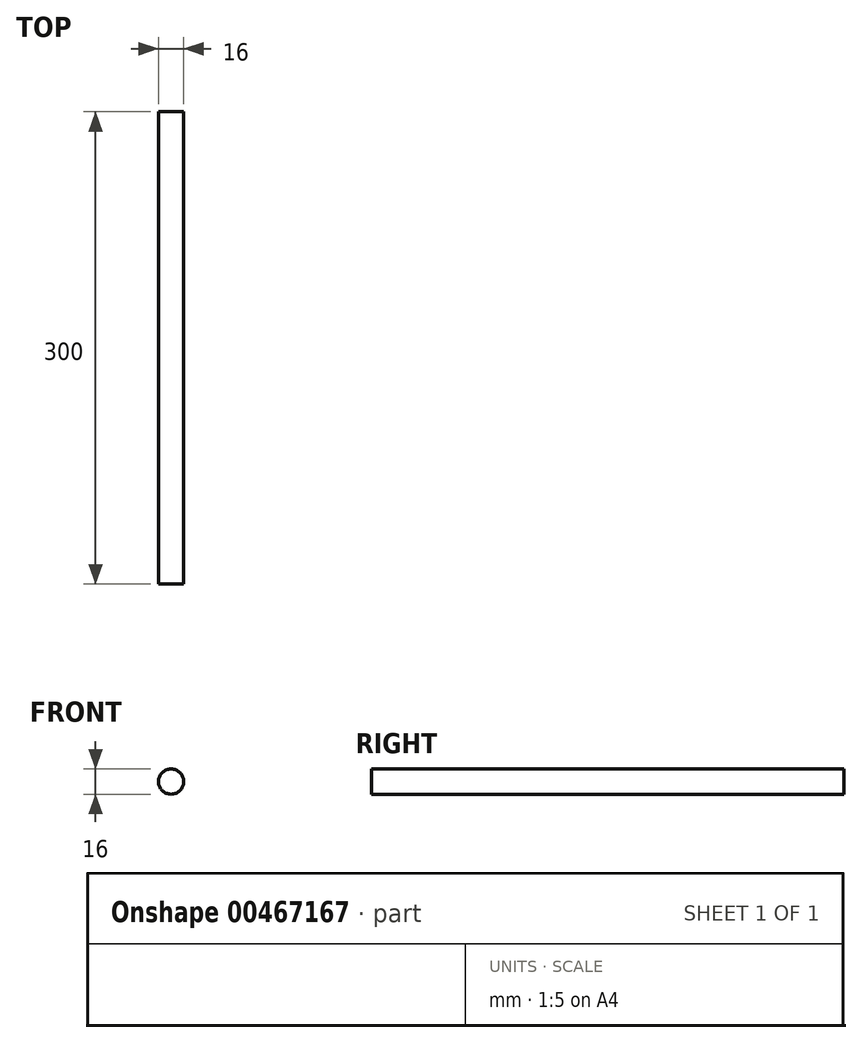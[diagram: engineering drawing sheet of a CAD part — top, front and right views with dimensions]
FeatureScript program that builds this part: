
annotation { "Feature Type Name" : "Feature", "Feature Type Description" : "" }
export const myFeature = defineFeature(function(context is Context, id is Id, definition is map)
    precondition{}
    {
        {
            assignVariable(context, id + "F0", {"name" : "Shaft_length", "anyValue" : 300 * mm});
        }
        {
            var Q0;
            Q0=qCreatedBy(makeId("Front.planeOp"),FACE);
            var sketch = newSketch(context, id + "F1", { "sketchPlane" : qUnion([Q0])});
            skCircle(sketch, "E0", {"center": v(0, 0) * mm, "radius": 8 * mm});
            skSolve(sketch);
        }
        {
            var Q0;
            Q0=qSketchRegion(id+"F1",true);
            extrude(context, id + "F2", {"entities" : qUnion([Q0]), "oppositeDirection" : true, "depth" : getVariable(context, 'Shaft_length')});
        }
    });
